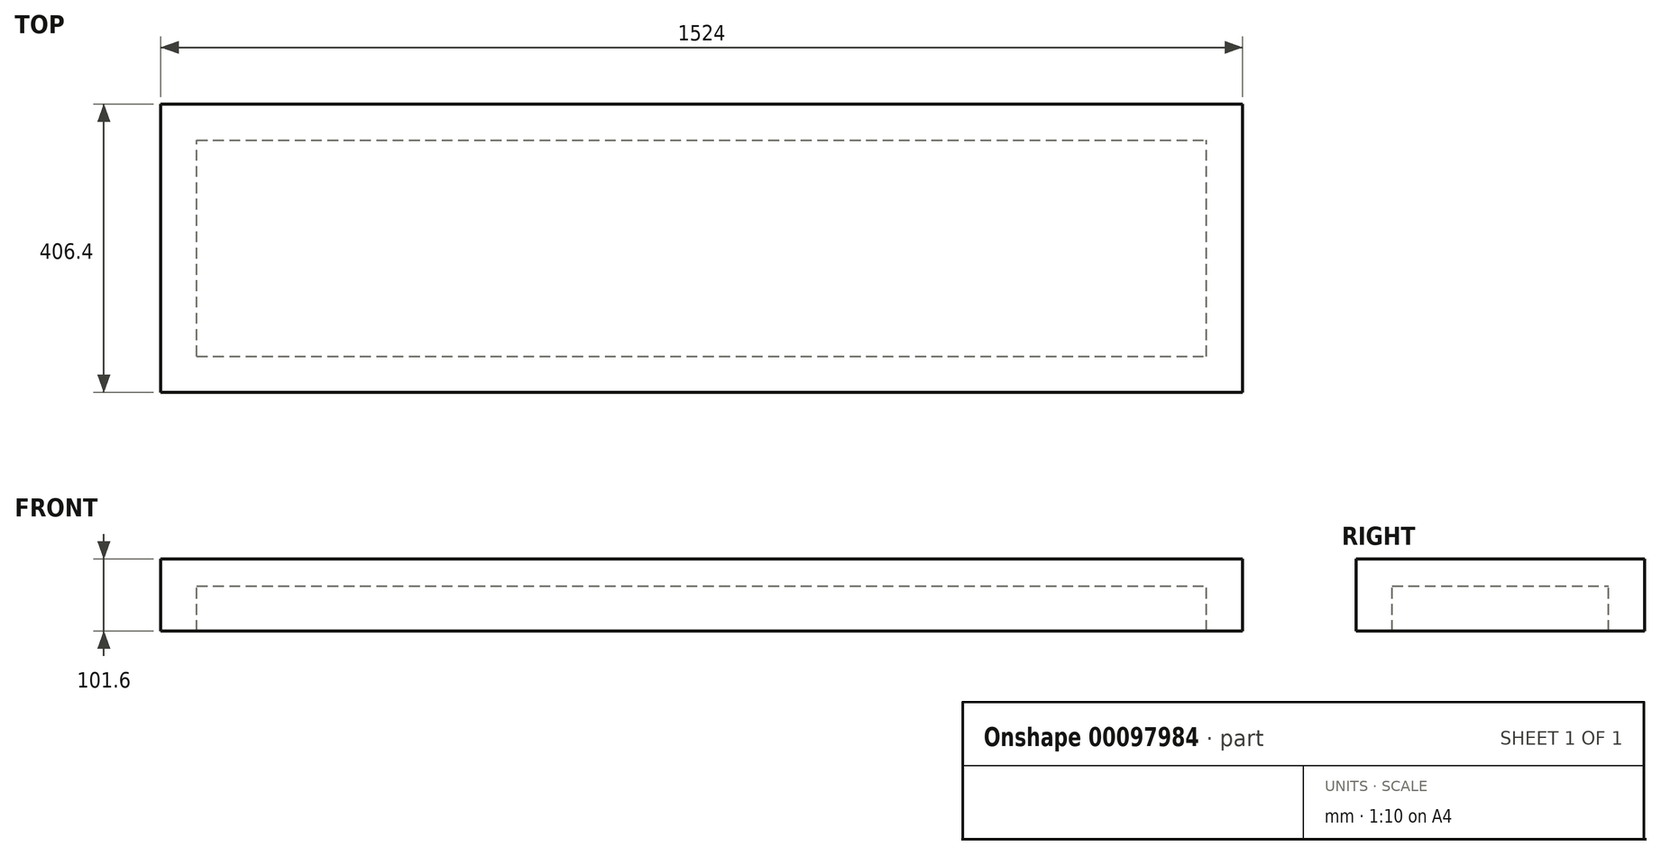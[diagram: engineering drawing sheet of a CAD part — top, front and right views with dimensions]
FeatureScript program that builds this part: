
annotation { "Feature Type Name" : "Feature", "Feature Type Description" : "" }
export const myFeature = defineFeature(function(context is Context, id is Id, definition is map)
    precondition{}
    {
        {
            var Q0;
            Q0=qCreatedBy(makeId("Top.planeOp"),FACE);
            var sketch = newSketch(context, id + "F0", { "sketchPlane" : qUnion([Q0])});
            skLineSegment(sketch, "E0.bottom", {"start": v(762, -203.2) * mm, "end": v(-762, -203.2) * mm});
            skLineSegment(sketch, "E0.top", {"start": v(762, 203.2) * mm, "end": v(-762, 203.2) * mm});
            skLineSegment(sketch, "E0.left", {"start": v(762, -203.2) * mm, "end": v(762, 203.2) * mm});
            skLineSegment(sketch, "E0.right", {"start": v(-762, -203.2) * mm, "end": v(-762, 203.2) * mm});
            skPoint(sketch, "E0.middle", {"position": v(0, 0) * mm});
            skSolve(sketch);
        }
        {
            var Q0;
            Q0=makeQuery(id+"F0.imprint","IMPRINT",FACE,{"disambiguationData":[TD([[makeQuery(id+"F0.imprint","IMPRINT",EDGE,{"derivedFrom":sQuery(id+"F0.wireOp",EDGE,"E0.bottom")}),-1.0]])]});
            extrude(context, id + "F1", {"entities" : qUnion([Q0]), "depth" : 38.1 * mm});
        }
        {
            var Q0;
            Q0=makeQuery(id+"F1.opExtrude","CAP_FACE",FACE,{"disambiguationData":[OSD([sQuery(id+"F0.wireOp",EDGE,"E0.bottom"),sQuery(id+"F0.wireOp",EDGE,"E0.top"),sQuery(id+"F0.wireOp",EDGE,"E0.left"),sQuery(id+"F0.wireOp",EDGE,"E0.right")])],"isStart":true});
            var sketch = newSketch(context, id + "F2", { "sketchPlane" : qUnion([Q0])});
            skLineSegment(sketch, "E1.bottom", {"start": v(762, 203.2) * mm, "end": v(711.2, 203.2) * mm});
            skLineSegment(sketch, "E1.top", {"start": v(762, -203.2) * mm, "end": v(711.2, -203.2) * mm});
            skLineSegment(sketch, "E1.left", {"start": v(762, 203.2) * mm, "end": v(762, -203.2) * mm});
            skLineSegment(sketch, "E1.right", {"start": v(711.2, 203.2) * mm, "end": v(711.2, -203.2) * mm});
            skLineSegment(sketch, "E2.bottom", {"start": v(-762, 203.2) * mm, "end": v(-711.2, 203.2) * mm});
            skLineSegment(sketch, "E2.top", {"start": v(-762, -203.2) * mm, "end": v(-711.2, -203.2) * mm});
            skLineSegment(sketch, "E2.left", {"start": v(-762, 203.2) * mm, "end": v(-762, -203.2) * mm});
            skLineSegment(sketch, "E2.right", {"start": v(-711.2, 203.2) * mm, "end": v(-711.2, -203.2) * mm});
            skLineSegment(sketch, "E3.bottom", {"start": v(-711.2, 203.2) * mm, "end": v(711.2, 203.2) * mm});
            skLineSegment(sketch, "E3.left", {"start": v(-711.2, 203.2) * mm, "end": v(-711.2, 152.4) * mm});
            skLineSegment(sketch, "E3.right", {"start": v(711.2, 203.2) * mm, "end": v(711.2, 152.4) * mm});
            skLineSegment(sketch, "E4.bottom", {"start": v(-711.2, -203.2) * mm, "end": v(711.2, -203.2) * mm});
            skLineSegment(sketch, "E4.top", {"start": v(-711.2, -152.4) * mm, "end": v(711.2, -152.4) * mm});
            skLineSegment(sketch, "E4.left", {"start": v(-711.2, -203.2) * mm, "end": v(-711.2, -152.4) * mm});
            skLineSegment(sketch, "E4.right", {"start": v(711.2, -203.2) * mm, "end": v(711.2, -152.4) * mm});
            skLineSegment(sketch, "E5.top", {"start": v(-711.2, 152.4) * mm, "end": v(711.2, 152.4) * mm});
            skSolve(sketch);
        }
        {
            var Q0;
            Q0=makeQuery(id+"F2.imprint","IMPRINT",FACE,{"disambiguationData":[TD([[makeQuery(id+"F2.imprint","IMPRINT",EDGE,{"derivedFrom":sQuery(id+"F2.wireOp",EDGE,"E2.bottom")}),1.0]])]});
            var Q1;
            Q1=makeQuery(id+"F2.imprint","IMPRINT",FACE,{"disambiguationData":[TD([[makeQuery(id+"F2.imprint","IMPRINT",EDGE,{"derivedFrom":sQuery(id+"F2.wireOp",EDGE,"E1.bottom")}),1.0]])]});
            var Q2;
            Q2=makeQuery(id+"F2.imprint","IMPRINT",FACE,{"disambiguationData":[TD([[makeQuery(id+"F2.imprint","IMPRINT",EDGE,{"derivedFrom":sQuery(id+"F2.wireOp",EDGE,"E4.bottom")}),-1.0]])]});
            var Q3;
            Q3=makeQuery(id+"F2.imprint","IMPRINT",FACE,{"disambiguationData":[TD([[makeQuery(id+"F2.imprint","IMPRINT",EDGE,{"derivedFrom":sQuery(id+"F2.wireOp",EDGE,"E3.bottom")}),1.0]])]});
            extrude(context, id + "F3", {"entities" : qUnion([Q0, Q1, Q2, Q3]), "operationType" : NewBodyOperationType.ADD, "depth" : 63.5 * mm});
        }
    });
